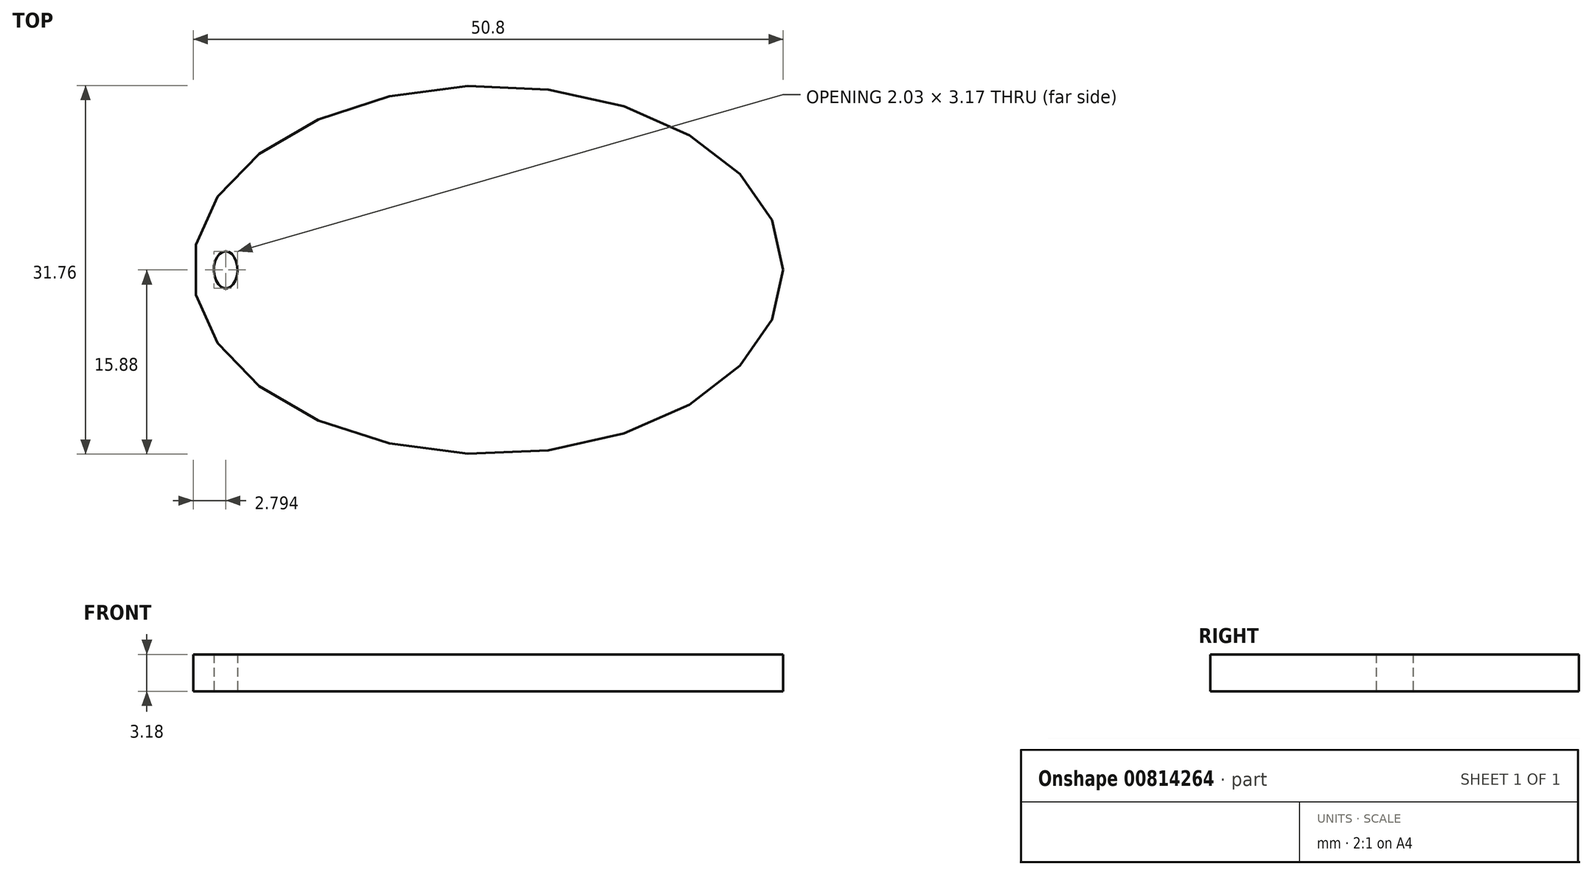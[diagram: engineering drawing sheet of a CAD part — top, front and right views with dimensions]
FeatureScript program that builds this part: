
annotation { "Feature Type Name" : "Feature", "Feature Type Description" : "" }
export const myFeature = defineFeature(function(context is Context, id is Id, definition is map)
    precondition{}
    {
        {
            var Q0;
            Q0=qCreatedBy(makeId("Top.planeOp"),FACE);
            var sketch = newSketch(context, id + "F0", { "sketchPlane" : qUnion([Q0])});
            skEllipse(sketch, "E0", {"center": v(0, 0) * mm, "majorRadius": 25.4 * mm, "minorRadius": 15.88 * mm, "majorAxis": v(1, 0)});
            skEllipse(sketch, "E1", {"center": v(-22.6, 0) * mm, "majorRadius": 1.02 * mm, "minorRadius": 1.59 * mm, "majorAxis": v(1, 0)});
            skSolve(sketch);
        }
        {
            var Q0;
            Q0=makeQuery(id+"F0.imprint","IMPRINT",FACE,{"disambiguationData":[TD([[makeQuery(id+"F0.imprint","IMPRINT",EDGE,{"derivedFrom":sQuery(id+"F0.wireOp",EDGE,"E0")}),1.0]])]});
            extrude(context, id + "F1", {"entities" : qUnion([Q0]), "depth" : 3.17 * mm, "offsetDistance" : 25.4 * mm});
        }
    });
